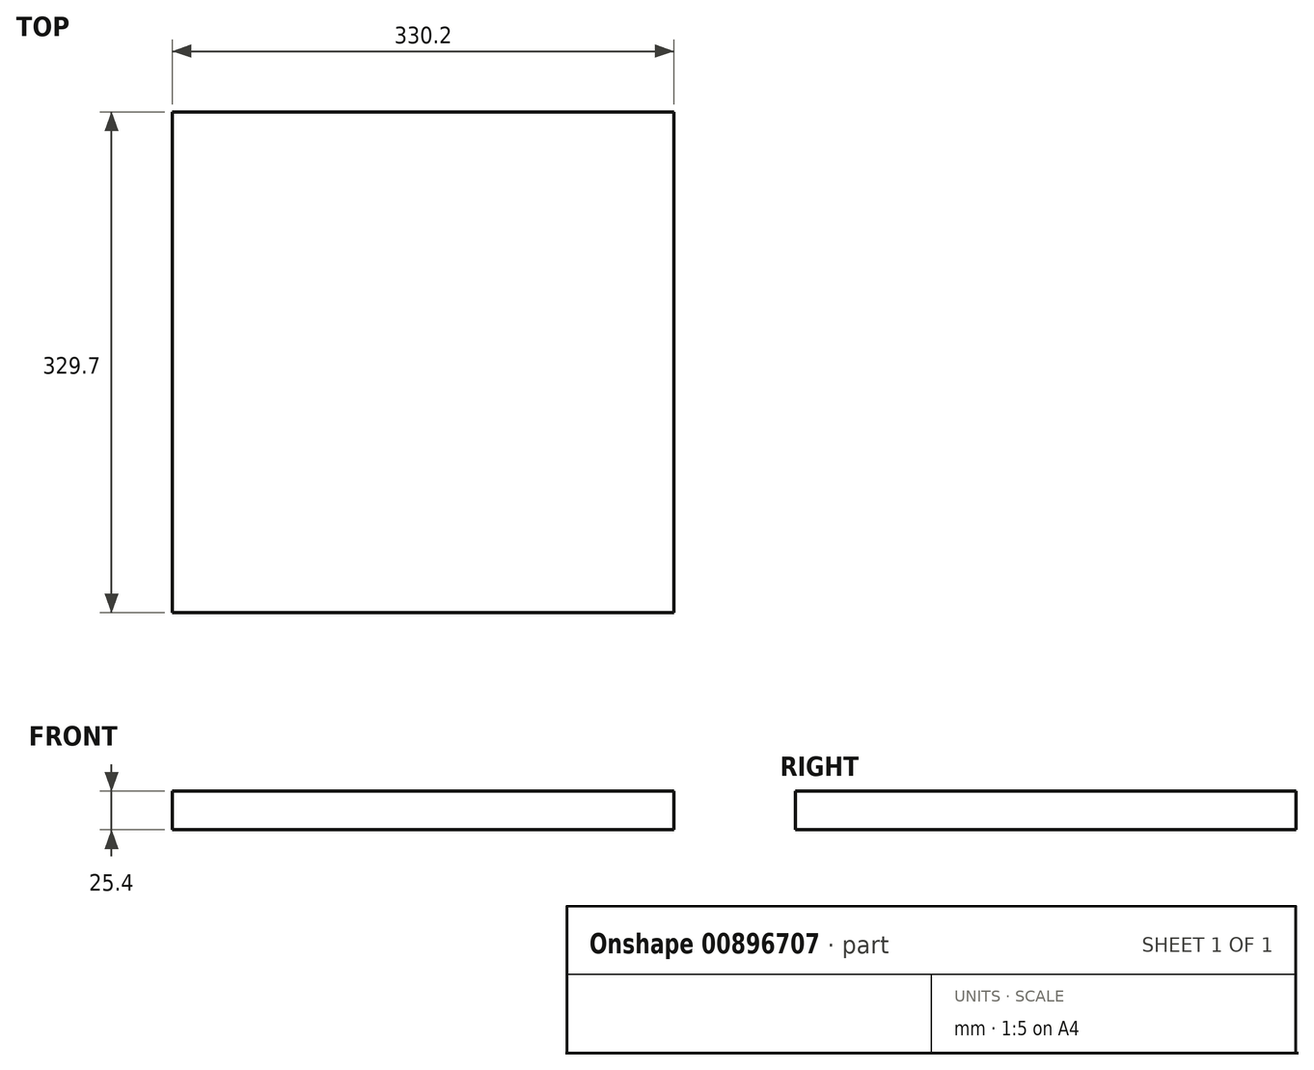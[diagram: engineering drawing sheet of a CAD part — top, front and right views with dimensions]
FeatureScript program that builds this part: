
annotation { "Feature Type Name" : "Feature", "Feature Type Description" : "" }
export const myFeature = defineFeature(function(context is Context, id is Id, definition is map)
    precondition{}
    {
        {
            var Q0;
            Q0=qCreatedBy(makeId("Front.planeOp"),FACE);
            var sketch = newSketch(context, id + "F0", { "sketchPlane" : qUnion([Q0])});
            skLineSegment(sketch, "E0.bottom", {"start": v(158.75, 12.7) * mm, "end": v(-158.75, 12.7) * mm});
            skLineSegment(sketch, "E0.top", {"start": v(158.75, -12.7) * mm, "end": v(-158.75, -12.7) * mm});
            skLineSegment(sketch, "E0.left", {"start": v(158.75, 12.7) * mm, "end": v(158.75, -12.7) * mm});
            skLineSegment(sketch, "E0.right", {"start": v(-158.75, 12.7) * mm, "end": v(-158.75, -12.7) * mm});
            skPoint(sketch, "E0.middle", {"position": v(0, 0) * mm});
            skLineSegment(sketch, "E1.bottom", {"start": v(158.75, 12.7) * mm, "end": v(165.1, 12.7) * mm});
            skLineSegment(sketch, "E1.top", {"start": v(158.75, -12.7) * mm, "end": v(165.1, -12.7) * mm});
            skLineSegment(sketch, "E1.right", {"start": v(165.1, 12.7) * mm, "end": v(165.1, -12.7) * mm});
            skLineSegment(sketch, "E2.bottom", {"start": v(-158.75, 12.7) * mm, "end": v(-165.1, 12.7) * mm});
            skLineSegment(sketch, "E2.top", {"start": v(-158.75, -12.7) * mm, "end": v(-165.1, -12.7) * mm});
            skLineSegment(sketch, "E2.right", {"start": v(-165.1, 12.7) * mm, "end": v(-165.1, -12.7) * mm});
            skSolve(sketch);
        }
        {
            var Q0;
            Q0 = qSketchRegion(id + "F0", true);
            extrude(context, id + "F1", {"entities" : qUnion([Q0]), "endBound" : BoundingType.SYMMETRIC, "depth" : 329.7 * mm, "offsetDistance" : 25.4 * mm});
        }
    });
